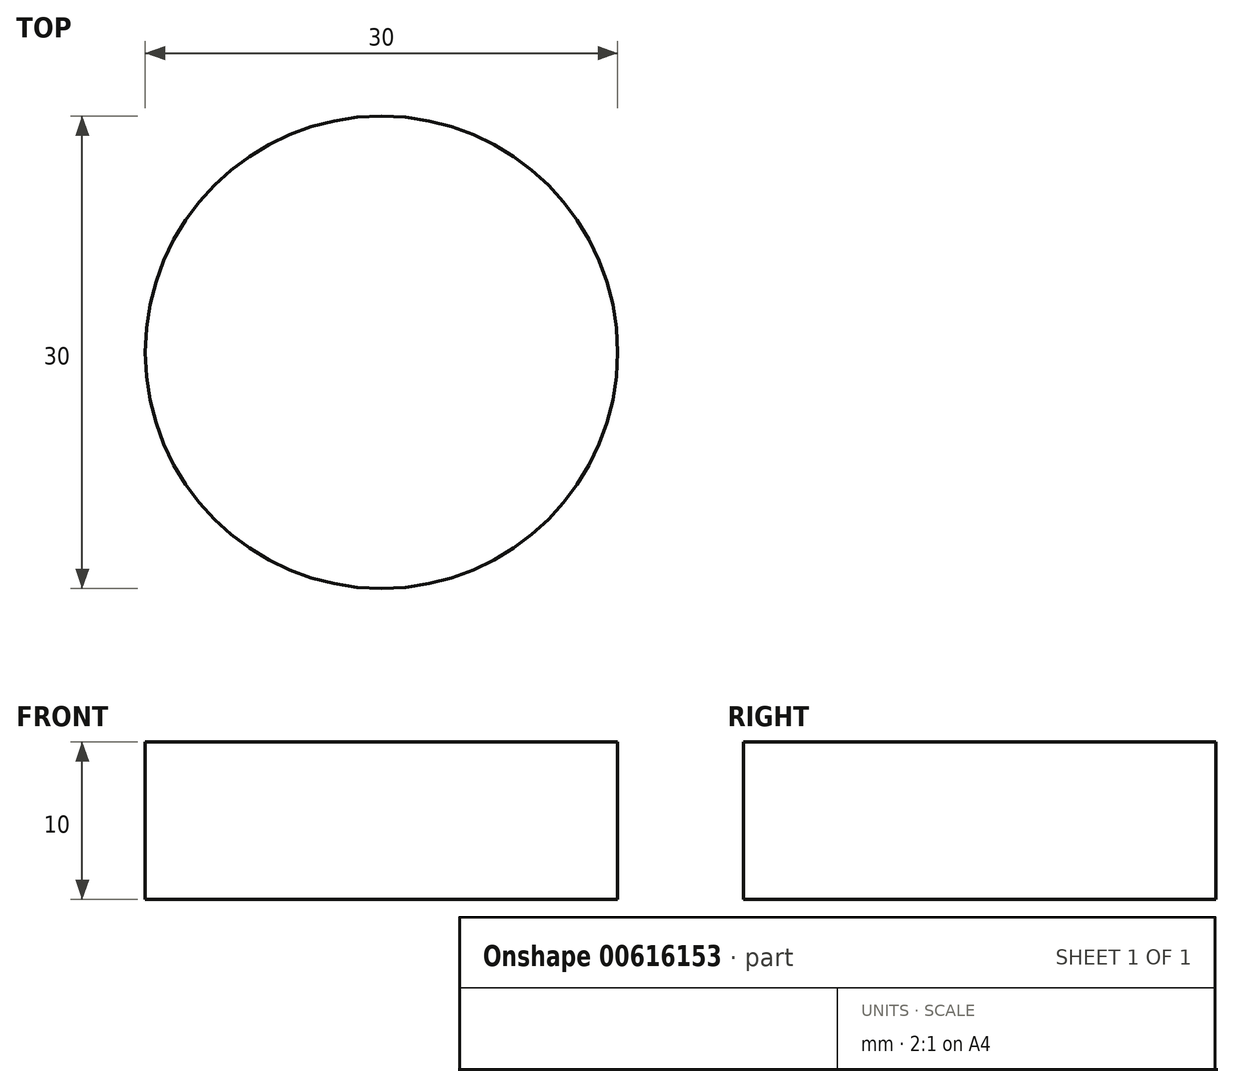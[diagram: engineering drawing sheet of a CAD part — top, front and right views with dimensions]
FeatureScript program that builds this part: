
annotation { "Feature Type Name" : "Feature", "Feature Type Description" : "" }
export const myFeature = defineFeature(function(context is Context, id is Id, definition is map)
    precondition{}
    {
        {
            var Q0;
            Q0=qCreatedBy(makeId("Top.planeOp"),FACE);
            var sketch = newSketch(context, id + "F0", { "sketchPlane" : qUnion([Q0])});
            skCircle(sketch, "E0", {"center": v(0, 0) * mm, "radius": 15 * mm});
            skSolve(sketch);
        }
        {
            var Q0;
            Q0=makeQuery(id+"F0.imprint","IMPRINT",FACE,{"disambiguationData":[TD([[makeQuery(id+"F0.imprint","IMPRINT",EDGE,{"derivedFrom":sQuery(id+"F0.wireOp",EDGE,"E0")}),1.0]])]});
            extrude(context, id + "F1", {"entities" : qUnion([Q0]), "depth" : 10 * mm, "offsetDistance" : 25 * mm});
        }
    });
